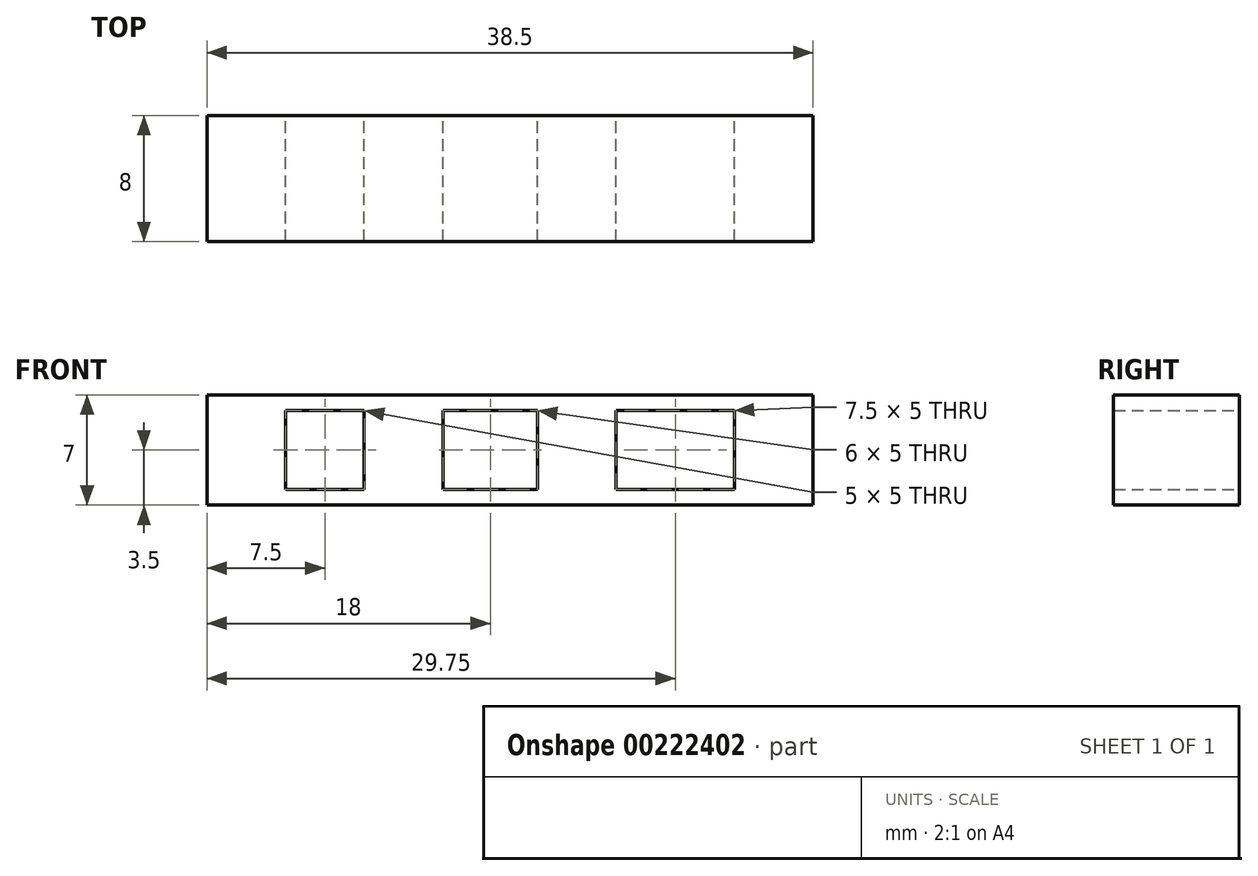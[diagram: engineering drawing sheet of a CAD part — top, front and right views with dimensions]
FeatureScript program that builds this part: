
annotation { "Feature Type Name" : "Feature", "Feature Type Description" : "" }
export const myFeature = defineFeature(function(context is Context, id is Id, definition is map)
    precondition{}
    {
        {
            var Q0;
            Q0=qCreatedBy(makeId("Top.planeOp"),FACE);
            var sketch = newSketch(context, id + "F0", { "sketchPlane" : qUnion([Q0])});
            skLineSegment(sketch, "E0.bottom", {"start": v(0, 0) * mm, "end": v(5, 0) * mm});
            skLineSegment(sketch, "E0.top", {"start": v(0, 8) * mm, "end": v(5, 8) * mm});
            skLineSegment(sketch, "E0.left", {"start": v(0, 0) * mm, "end": v(0, 8) * mm});
            skLineSegment(sketch, "E0.right", {"start": v(5, 0) * mm, "end": v(5, 8) * mm});
            skLineSegment(sketch, "E1.bottom", {"start": v(10, 0) * mm, "end": v(15, 0) * mm});
            skLineSegment(sketch, "E1.top", {"start": v(10, 8) * mm, "end": v(15, 8) * mm});
            skLineSegment(sketch, "E1.left", {"start": v(10, 0) * mm, "end": v(10, 8) * mm});
            skLineSegment(sketch, "E1.right", {"start": v(15, 0) * mm, "end": v(15, 8) * mm});
            skLineSegment(sketch, "E2.bottom", {"start": v(21, 0) * mm, "end": v(26, 0) * mm});
            skLineSegment(sketch, "E2.top", {"start": v(21, 8) * mm, "end": v(26, 8) * mm});
            skLineSegment(sketch, "E2.left", {"start": v(21, 0) * mm, "end": v(21, 8) * mm});
            skLineSegment(sketch, "E2.right", {"start": v(26, 0) * mm, "end": v(26, 8) * mm});
            skLineSegment(sketch, "E3.bottom", {"start": v(33.5, 0) * mm, "end": v(38.5, 0) * mm});
            skLineSegment(sketch, "E3.top", {"start": v(33.5, 8) * mm, "end": v(38.5, 8) * mm});
            skLineSegment(sketch, "E3.left", {"start": v(33.5, 0) * mm, "end": v(33.5, 8) * mm});
            skLineSegment(sketch, "E3.right", {"start": v(38.5, 0) * mm, "end": v(38.5, 8) * mm});
            skSolve(sketch);
        }
        {
            var Q0;
            Q0 = qSketchRegion(id + "F0", true);
            extrude(context, id + "F1", {"entities" : qUnion([Q0]), "depth" : 5 * mm, "offsetDistance" : 25 * mm});
        }
        {
            var Q0;
            Q0=qCreatedBy(makeId("Top.planeOp"),FACE);
            var sketch = newSketch(context, id + "F2", { "sketchPlane" : qUnion([Q0])});
            skLineSegment(sketch, "E4.bottom", {"start": v(0, 0) * mm, "end": v(38.5, 0) * mm});
            skLineSegment(sketch, "E4.top", {"start": v(0, 8) * mm, "end": v(38.5, 8) * mm});
            skLineSegment(sketch, "E4.left", {"start": v(0, 0) * mm, "end": v(0, 8) * mm});
            skLineSegment(sketch, "E4.right", {"start": v(38.5, 0) * mm, "end": v(38.5, 8) * mm});
            skSolve(sketch);
        }
        {
            var Q0;
            Q0 = qSketchRegion(id + "F2", true);
            extrude(context, id + "F3", {"entities" : qUnion([Q0]), "operationType" : NewBodyOperationType.ADD, "oppositeDirection" : true, "depth" : 1 * mm, "offsetDistance" : 25 * mm});
        }
        {
            var Q0;
            Q0=makeQuery(id+"F1.opExtrude","CAP_FACE",FACE,{"disambiguationData":[OSD([sQuery(id+"F0.wireOp",EDGE,"E0.bottom"),sQuery(id+"F0.wireOp",EDGE,"E0.top"),sQuery(id+"F0.wireOp",EDGE,"E0.left"),sQuery(id+"F0.wireOp",EDGE,"E0.right")])],"isStart":false});
            var sketch = newSketch(context, id + "F4", { "sketchPlane" : qUnion([Q0])});
            skLineSegment(sketch, "E5.bottom", {"start": v(0, 8) * mm, "end": v(38.5, 8) * mm});
            skLineSegment(sketch, "E5.top", {"start": v(0, 0) * mm, "end": v(38.5, 0) * mm});
            skLineSegment(sketch, "E5.left", {"start": v(0, 8) * mm, "end": v(0, 0) * mm});
            skLineSegment(sketch, "E5.right", {"start": v(38.5, 8) * mm, "end": v(38.5, 0) * mm});
            skSolve(sketch);
        }
        {
            var Q0;
            Q0 = qSketchRegion(id + "F4", true);
            extrude(context, id + "F5", {"entities" : qUnion([Q0]), "operationType" : NewBodyOperationType.ADD, "depth" : 1 * mm, "offsetDistance" : 25 * mm});
        }
    });
